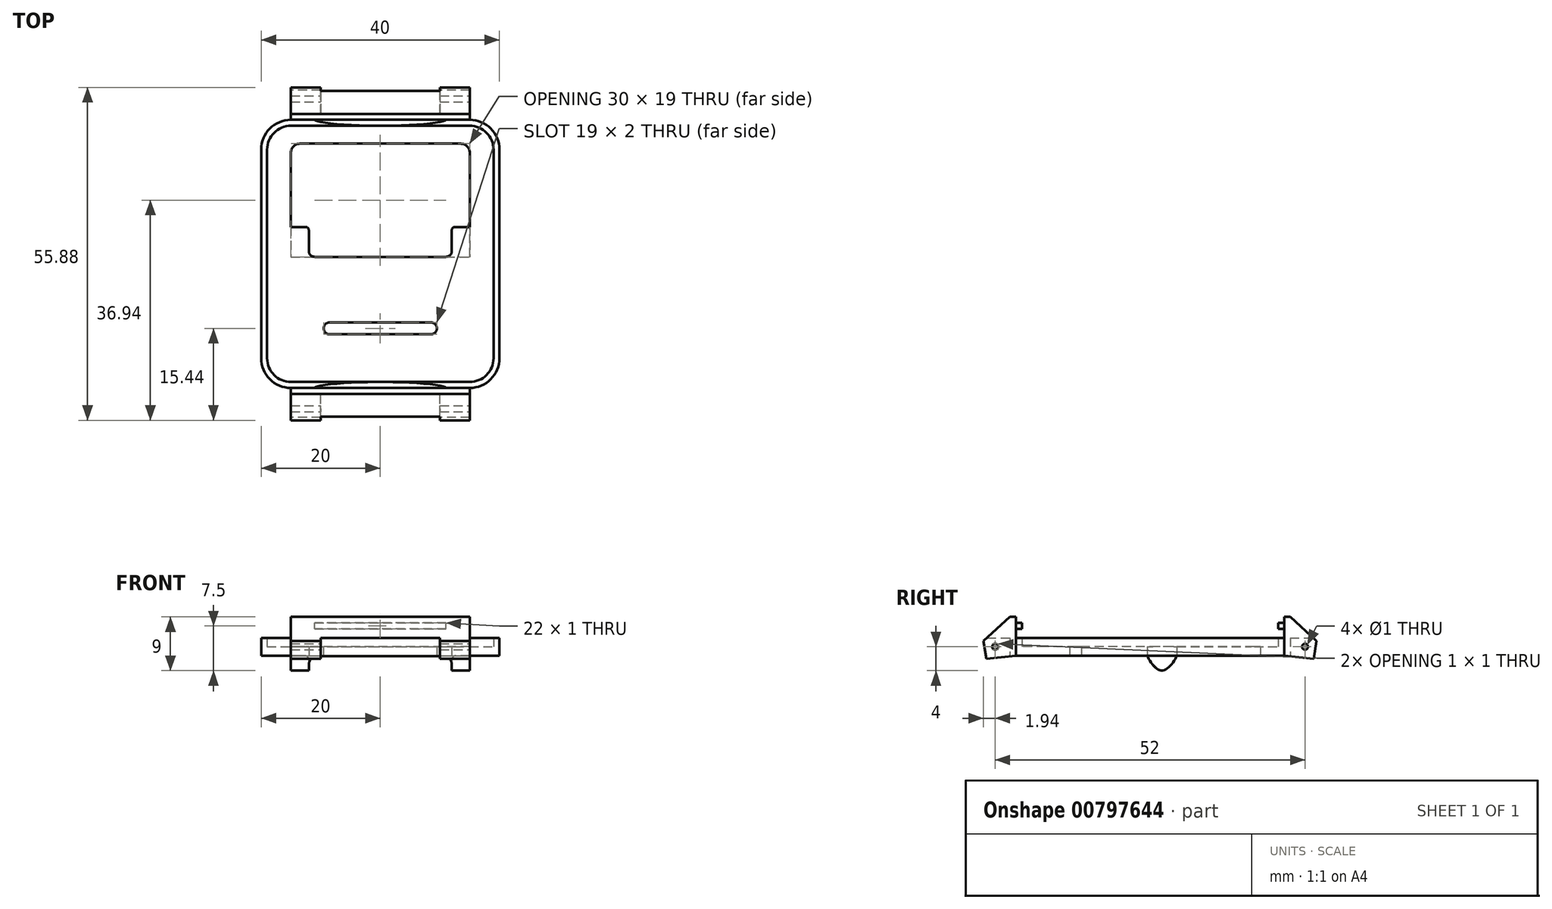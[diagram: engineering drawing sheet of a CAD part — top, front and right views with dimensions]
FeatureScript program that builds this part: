
annotation { "Feature Type Name" : "Feature", "Feature Type Description" : "" }
export const myFeature = defineFeature(function(context is Context, id is Id, definition is map)
    precondition{}
    {
        {
            var Q0;
            Q0=qCreatedBy(makeId("Top.planeOp"),FACE);
            var sketch = newSketch(context, id + "F0", { "sketchPlane" : qUnion([Q0])});
            skLineSegment(sketch, "E0.bottom", {"start": v(-20, -22.5) * mm, "end": v(20, -22.5) * mm});
            skLineSegment(sketch, "E0.top", {"start": v(-20, 22.5) * mm, "end": v(20, 22.5) * mm});
            skLineSegment(sketch, "E0.left", {"start": v(-20, -22.5) * mm, "end": v(-20, 22.5) * mm});
            skLineSegment(sketch, "E0.right", {"start": v(20, -22.5) * mm, "end": v(20, 22.5) * mm});
            skPoint(sketch, "E1", {"position": v(0, 22.5) * mm});
            skPoint(sketch, "E2", {"position": v(20, 0) * mm});
            skLineSegment(sketch, "E3.bottom", {"start": v(-15, 4.5) * mm, "end": v(15, 4.5) * mm});
            skLineSegment(sketch, "E3.top", {"start": v(-15, 18.5) * mm, "end": v(15, 18.5) * mm});
            skLineSegment(sketch, "E3.left", {"start": v(-15, 4.5) * mm, "end": v(-15, 18.5) * mm});
            skLineSegment(sketch, "E3.right", {"start": v(15, 4.5) * mm, "end": v(15, 18.5) * mm});
            skLineSegment(sketch, "E4.bottom", {"start": v(-9.5, -13.5) * mm, "end": v(9.5, -13.5) * mm});
            skLineSegment(sketch, "E4.top", {"start": v(-9.5, -11.5) * mm, "end": v(9.5, -11.5) * mm});
            skLineSegment(sketch, "E4.left", {"start": v(-9.5, -13.5) * mm, "end": v(-9.5, -11.5) * mm});
            skLineSegment(sketch, "E4.right", {"start": v(9.5, -13.5) * mm, "end": v(9.5, -11.5) * mm});
            skPoint(sketch, "E5", {"position": v(0, -11.5) * mm});
            skLineSegment(sketch, "E6.bottom", {"start": v(-12, 4.5) * mm, "end": v(12, 4.5) * mm});
            skLineSegment(sketch, "E6.top", {"start": v(-12, -0.5) * mm, "end": v(12, -0.5) * mm});
            skLineSegment(sketch, "E6.left", {"start": v(-12, 4.5) * mm, "end": v(-12, -0.5) * mm});
            skLineSegment(sketch, "E6.right", {"start": v(12, 4.5) * mm, "end": v(12, -0.5) * mm});
            skLineSegment(sketch, "E7.bottom", {"start": v(-15, 4.5) * mm, "end": v(-12, 4.5) * mm});
            skLineSegment(sketch, "E7.top", {"start": v(-15, -0.5) * mm, "end": v(-12, -0.5) * mm});
            skLineSegment(sketch, "E7.left", {"start": v(-15, 4.5) * mm, "end": v(-15, -0.5) * mm});
            skLineSegment(sketch, "E8.bottom", {"start": v(12, -0.5) * mm, "end": v(15, -0.5) * mm});
            skLineSegment(sketch, "E8.top", {"start": v(12, 4.5) * mm, "end": v(15, 4.5) * mm});
            skLineSegment(sketch, "E8.left", {"start": v(12, -0.5) * mm, "end": v(12, 4.5) * mm});
            skLineSegment(sketch, "E8.right", {"start": v(15, -0.5) * mm, "end": v(15, 4.5) * mm});
            skSolve(sketch);
        }
        {
            var Q0;
            Q0=makeQuery(id+"F0.imprint","IMPRINT",FACE,{"disambiguationData":[TD([[makeQuery(id+"F0.imprint","IMPRINT",EDGE,{"derivedFrom":sQuery(id+"F0.wireOp",EDGE,"E0.bottom")}),1.0]])]});
            var Q1;
            {var subQ0=sQuery(id+"F0.wireOp",EDGE,"E6.left");Q1=makeQuery(id+"F0.imprint","IMPRINT",FACE,{"disambiguationData":[TD([[makeQuery(id+"F0.imprint","IMPRINT",EDGE,{"derivedFrom":subQ0}),-1.0]])]});}
            var Q2;
            {var subQ2=sQuery(id+"F0.wireOp",EDGE,"E6.right");Q2=makeQuery(id+"F0.imprint","IMPRINT",FACE,{"disambiguationData":[TD([[makeQuery(id+"F0.imprint","IMPRINT",EDGE,{"derivedFrom":subQ2}),1.0]])]});}
            extrude(context, id + "F1", {"entities" : qUnion([Q0, Q1, Q2]), "depth" : 1.5 * mm, "offsetDistance" : 25 * mm});
        }
        {
            var Q0;
            {var subQ2=sQuery(id+"F0.wireOp",EDGE,"E6.right");Q0=makeQuery(id+"F0.imprint","IMPRINT",FACE,{"disambiguationData":[TD([[makeQuery(id+"F0.imprint","IMPRINT",EDGE,{"derivedFrom":subQ2}),1.0]])]});}
            var Q1;
            {var subQ0=sQuery(id+"F0.wireOp",EDGE,"E6.left");Q1=makeQuery(id+"F0.imprint","IMPRINT",FACE,{"disambiguationData":[TD([[makeQuery(id+"F0.imprint","IMPRINT",EDGE,{"derivedFrom":subQ0}),-1.0]])]});}
            extrude(context, id + "F2", {"entities" : qUnion([Q0, Q1]), "operationType" : NewBodyOperationType.ADD, "oppositeDirection" : true, "depth" : 2.5 * mm, "offsetDistance" : 25 * mm});
        }
        {
            var Q0;
            Q0=makeQuery(id+"F2.opExtrude","SWEPT_FACE",FACE,{"disambiguationData":[OSD([sQuery(id+"F0.wireOp",EDGE,"E7.left")])]});
            var sketch = newSketch(context, id + "F3", { "sketchPlane" : qUnion([Q0])});
            skPoint(sketch, "E9", {"position": v(-2, -2.5) * mm});
            skPoint(sketch, "E10", {"position": v(-4.5, 0) * mm});
            skPoint(sketch, "E11", {"position": v(0.5, 0) * mm});
            skPoint(sketch, "E12", {"position": v(-2, 4.5) * mm});
            skPoint(sketch, "E12.positionSnap0", {"position": v(-2, 0) * mm});
            skPoint(sketch, "E13", {"position": v(0.5, 2) * mm});
            skPoint(sketch, "E14", {"position": v(-4.5, 2) * mm});
            skFitSpline(sketch, "E15", {"points": [v(-4.5, 0) * mm, v(-2, -2.5) * mm, v(0.5, 0) * mm, v(0.5, 2) * mm, v(-2, 4.5) * mm, v(-4.5, 2) * mm, v(-4.5, 0) * mm]});
            skSolve(sketch);
        }
        {
            var Q0;
            {var subQ1=sQuery(id+"F0.wireOp",EDGE,"E7.left");var subQ2=makeQuery(id+"F2.opExtrude","SWEPT_EDGE",EDGE,{"disambiguationData":[OSD([sQuery(id+"F0.wireOp",EDGE,"E3.bottom"),sQuery(id+"F0.wireOp",EDGE,"E3.left"),subQ1])]});Q0=makeQuery(id+"F3.imprint","IMPRINT",FACE,{"disambiguationData":[TD([[makeQuery(id+"F3.imprint","IMPRINT",EDGE,{"derivedFrom":subQ2}),-1.0]])]});}
            var Q1;
            {var subQ1=sQuery(id+"F0.wireOp",EDGE,"E7.left");var subQ2=makeQuery(id+"F2.opExtrude","SWEPT_EDGE",EDGE,{"disambiguationData":[OSD([sQuery(id+"F0.wireOp",EDGE,"E7.top"),subQ1])]});Q1=makeQuery(id+"F3.imprint","IMPRINT",FACE,{"disambiguationData":[TD([[makeQuery(id+"F3.imprint","IMPRINT",EDGE,{"derivedFrom":subQ2}),1.0]])]});}
            extrude(context, id + "F4", {"entities" : qUnion([Q0, Q1]), "operationType" : NewBodyOperationType.REMOVE, "oppositeDirection" : true, "depth" : 50 * mm, "offsetDistance" : 25 * mm});
        }
        {
            var Q0;
            Q0=makeQuery(id+"F1.opExtrude","SWEPT_EDGE",EDGE,{"disambiguationData":[OSD([sQuery(id+"F0.wireOp",EDGE,"E4.top"),sQuery(id+"F0.wireOp",EDGE,"E4.right")])]});
            var Q1;
            Q1=makeQuery(id+"F1.opExtrude","SWEPT_EDGE",EDGE,{"disambiguationData":[OSD([sQuery(id+"F0.wireOp",EDGE,"E4.bottom"),sQuery(id+"F0.wireOp",EDGE,"E4.right")])]});
            var Q2;
            Q2=makeQuery(id+"F1.opExtrude","SWEPT_EDGE",EDGE,{"disambiguationData":[OSD([sQuery(id+"F0.wireOp",EDGE,"E4.top"),sQuery(id+"F0.wireOp",EDGE,"E4.left")])]});
            var Q3;
            Q3=makeQuery(id+"F1.opExtrude","SWEPT_EDGE",EDGE,{"disambiguationData":[OSD([sQuery(id+"F0.wireOp",EDGE,"E4.bottom"),sQuery(id+"F0.wireOp",EDGE,"E4.left")])]});
            fillet(context, id + "F5", {"entities" : qUnion([Q0, Q1, Q2, Q3]), "radius" : 1 * mm, "tangentPropagation" : true, "allowEdgeOverflow" : false});
        }
        {
            var Q0;
            Q0=makeQuery(id+"F1.opExtrude","SWEPT_EDGE",EDGE,{"disambiguationData":[OSD([sQuery(id+"F0.wireOp",EDGE,"E3.top"),sQuery(id+"F0.wireOp",EDGE,"E3.left")])]});
            var Q1;
            Q1=makeQuery(id+"F1.opExtrude","SWEPT_EDGE",EDGE,{"disambiguationData":[OSD([sQuery(id+"F0.wireOp",EDGE,"E3.top"),sQuery(id+"F0.wireOp",EDGE,"E3.right")])]});
            fillet(context, id + "F6", {"entities" : qUnion([Q0, Q1]), "radius" : 1.5 * mm, "tangentPropagation" : true, "allowEdgeOverflow" : false});
        }
        {
            var Q0;
            Q0=makeQuery(id+"F1.opExtrude","SWEPT_EDGE",EDGE,{"disambiguationData":[OSD([sQuery(id+"F0.wireOp",EDGE,"E6.top"),sQuery(id+"F0.wireOp",EDGE,"E6.right"),sQuery(id+"F0.wireOp",EDGE,"E8.bottom")])]});
            var Q1;
            Q1=makeQuery(id+"F1.opExtrude","SWEPT_EDGE",EDGE,{"disambiguationData":[OSD([sQuery(id+"F0.wireOp",EDGE,"E6.top"),sQuery(id+"F0.wireOp",EDGE,"E6.left"),sQuery(id+"F0.wireOp",EDGE,"E7.top")])]});
            fillet(context, id + "F7", {"entities" : qUnion([Q0, Q1]), "radius" : 1 * mm, "tangentPropagation" : true, "allowEdgeOverflow" : false});
        }
        {
            var Q0;
            {var subQ0=sQuery(id+"F0.wireOp",EDGE,"E6.right");var subQ1=sQuery(id+"F0.wireOp",EDGE,"E3.bottom");Q0=makeQuery(id+"F2.boolean.opBoolean","MERGE",EDGE,{"derivedFrom":[makeQuery(id+"F1.opExtrude","SWEPT_EDGE",EDGE,{"disambiguationData":[OSD([subQ1,subQ0])]}),makeQuery(id+"F2.opExtrude","SWEPT_EDGE",EDGE,{"disambiguationData":[OSD([subQ1,subQ0])]})]});}
            var Q1;
            {var subQ0=sQuery(id+"F0.wireOp",EDGE,"E6.left");var subQ1=sQuery(id+"F0.wireOp",EDGE,"E3.bottom");Q1=makeQuery(id+"F2.boolean.opBoolean","MERGE",EDGE,{"derivedFrom":[makeQuery(id+"F1.opExtrude","SWEPT_EDGE",EDGE,{"disambiguationData":[OSD([subQ1,subQ0])]}),makeQuery(id+"F2.opExtrude","SWEPT_EDGE",EDGE,{"disambiguationData":[OSD([subQ1,subQ0])]})]});}
            fillet(context, id + "F8", {"entities" : qUnion([Q0, Q1]), "radius" : 0.5 * mm, "tangentPropagation" : true, "allowEdgeOverflow" : false});
        }
        {
            var Q0;
            Q0=qCreatedBy(makeId("Top.planeOp"),FACE);
            var sketch = newSketch(context, id + "F9", { "sketchPlane" : qUnion([Q0])});
            skLineSegment(sketch, "E16.bottom", {"start": v(-20, -22.5) * mm, "end": v(20, -22.5) * mm});
            skLineSegment(sketch, "E16.top", {"start": v(-20, 22.5) * mm, "end": v(20, 22.5) * mm});
            skLineSegment(sketch, "E16.left", {"start": v(-20, -22.5) * mm, "end": v(-20, 22.5) * mm});
            skLineSegment(sketch, "E16.right", {"start": v(20, -22.5) * mm, "end": v(20, 22.5) * mm});
            skPoint(sketch, "E17", {"position": v(0, 22.5) * mm});
            skPoint(sketch, "E18.positionSnap0", {"position": v(20, 0) * mm});
            skLineSegment(sketch, "E19.bottom", {"start": v(-19, -21.5) * mm, "end": v(19, -21.5) * mm});
            skLineSegment(sketch, "E19.top", {"start": v(-19, 21.5) * mm, "end": v(19, 21.5) * mm});
            skLineSegment(sketch, "E19.left", {"start": v(-19, -21.5) * mm, "end": v(-19, 21.5) * mm});
            skLineSegment(sketch, "E19.right", {"start": v(19, -21.5) * mm, "end": v(19, 21.5) * mm});
            skSolve(sketch);
        }
        {
            var Q0;
            Q0 = qSketchRegion(id + "F9", true);
            extrude(context, id + "F10", {"entities" : qUnion([Q0]), "operationType" : NewBodyOperationType.ADD, "depth" : 3 * mm, "offsetDistance" : 25 * mm});
        }
        {
            var Q0;
            Q0=makeQuery(id+"F10.opExtrude","SWEPT_EDGE",EDGE,{"disambiguationData":[OSD([sQuery(id+"F9.wireOp",EDGE,"E19.top"),sQuery(id+"F9.wireOp",EDGE,"E19.left")])]});
            var Q1;
            Q1=makeQuery(id+"F10.opExtrude","SWEPT_EDGE",EDGE,{"disambiguationData":[OSD([sQuery(id+"F9.wireOp",EDGE,"E19.top"),sQuery(id+"F9.wireOp",EDGE,"E19.right")])]});
            var Q2;
            Q2=makeQuery(id+"F10.opExtrude","SWEPT_EDGE",EDGE,{"disambiguationData":[OSD([sQuery(id+"F9.wireOp",EDGE,"E19.bottom"),sQuery(id+"F9.wireOp",EDGE,"E19.right")])]});
            var Q3;
            Q3=makeQuery(id+"F10.opExtrude","SWEPT_EDGE",EDGE,{"disambiguationData":[OSD([sQuery(id+"F9.wireOp",EDGE,"E19.bottom"),sQuery(id+"F9.wireOp",EDGE,"E19.left")])]});
            fillet(context, id + "F11", {"entities" : qUnion([Q0, Q1, Q2, Q3]), "radius" : 4 * mm, "tangentPropagation" : true, "allowEdgeOverflow" : false});
        }
        {
            var Q0;
            Q0=makeQuery(id+"F10.boolean.opBoolean","MERGE",EDGE,{"derivedFrom":[makeQuery(id+"F1.opExtrude","SWEPT_EDGE",EDGE,{"disambiguationData":[OSD([sQuery(id+"F0.wireOp",EDGE,"E0.bottom"),sQuery(id+"F0.wireOp",EDGE,"E0.left")])]}),makeQuery(id+"F10.opExtrude","SWEPT_EDGE",EDGE,{"disambiguationData":[OSD([sQuery(id+"F9.wireOp",EDGE,"E16.bottom"),sQuery(id+"F9.wireOp",EDGE,"E16.left")])]})]});
            var Q1;
            Q1=makeQuery(id+"F10.boolean.opBoolean","MERGE",EDGE,{"derivedFrom":[makeQuery(id+"F1.opExtrude","SWEPT_EDGE",EDGE,{"disambiguationData":[OSD([sQuery(id+"F0.wireOp",EDGE,"E0.bottom"),sQuery(id+"F0.wireOp",EDGE,"E0.right")])]}),makeQuery(id+"F10.opExtrude","SWEPT_EDGE",EDGE,{"disambiguationData":[OSD([sQuery(id+"F9.wireOp",EDGE,"E16.bottom"),sQuery(id+"F9.wireOp",EDGE,"E16.right")])]})]});
            var Q2;
            Q2=makeQuery(id+"F10.boolean.opBoolean","MERGE",EDGE,{"derivedFrom":[makeQuery(id+"F1.opExtrude","SWEPT_EDGE",EDGE,{"disambiguationData":[OSD([sQuery(id+"F0.wireOp",EDGE,"E0.top"),sQuery(id+"F0.wireOp",EDGE,"E0.right")])]}),makeQuery(id+"F10.opExtrude","SWEPT_EDGE",EDGE,{"disambiguationData":[OSD([sQuery(id+"F9.wireOp",EDGE,"E16.top"),sQuery(id+"F9.wireOp",EDGE,"E16.right")])]})]});
            var Q3;
            Q3=makeQuery(id+"F10.boolean.opBoolean","MERGE",EDGE,{"derivedFrom":[makeQuery(id+"F1.opExtrude","SWEPT_EDGE",EDGE,{"disambiguationData":[OSD([sQuery(id+"F0.wireOp",EDGE,"E0.top"),sQuery(id+"F0.wireOp",EDGE,"E0.left")])]}),makeQuery(id+"F10.opExtrude","SWEPT_EDGE",EDGE,{"disambiguationData":[OSD([sQuery(id+"F9.wireOp",EDGE,"E16.top"),sQuery(id+"F9.wireOp",EDGE,"E16.left")])]})]});
            fillet(context, id + "F12", {"entities" : qUnion([Q0, Q1, Q2, Q3]), "radius" : 5 * mm, "tangentPropagation" : true, "allowEdgeOverflow" : false});
        }
        {
            var Q0;
            Q0=qCreatedBy(makeId("Right.planeOp"),FACE);
            var sketch = newSketch(context, id + "F13", { "sketchPlane" : qUnion([Q0])});
            skLineSegment(sketch, "E20", {"start": v(22.5, 0) * mm, "end": v(-22.5, 0) * mm, "construction": true});
            skPoint(sketch, "E21", {"position": v(0, 0) * mm});
            skLineSegment(sketch, "E22", {"start": v(22.5, 0) * mm, "end": v(27.47, -0.5) * mm});
            skLineSegment(sketch, "E23", {"start": v(22.5, 0) * mm, "end": v(22.5, 6.5) * mm});
            skLineSegment(sketch, "E24", {"start": v(22.5, 6.5) * mm, "end": v(23.5, 6.5) * mm});
            skLineSegment(sketch, "E25", {"start": v(23.5, 6.5) * mm, "end": v(27.94, 2.46) * mm});
            skLineSegment(sketch, "E26", {"start": v(27.47, -0.5) * mm, "end": v(27.94, 2.46) * mm});
            skLineSegment(sketch, "E27", {"start": v(-22.5, 0) * mm, "end": v(-27.47, -0.5) * mm});
            skLineSegment(sketch, "E28", {"start": v(-27.47, -0.5) * mm, "end": v(-27.94, 2.46) * mm});
            skLineSegment(sketch, "E29", {"start": v(-22.5, 0) * mm, "end": v(-22.5, 6.5) * mm});
            skLineSegment(sketch, "E30", {"start": v(-22.5, 6.5) * mm, "end": v(-23.5, 6.5) * mm});
            skLineSegment(sketch, "E31", {"start": v(-23.5, 6.5) * mm, "end": v(-27.94, 2.46) * mm});
            skSolve(sketch);
        }
        {
            var Q0;
            Q0 = qSketchRegion(id + "F13", true);
            extrude(context, id + "F14", {"entities" : qUnion([Q0]), "operationType" : NewBodyOperationType.ADD, "depth" : 15 * mm, "offsetDistance" : 25 * mm, "hasSecondDirection" : true, "secondDirectionOppositeDirection" : true, "secondDirectionDepth" : 15 * mm});
        }
        {
            var Q0;
            Q0=makeQuery(id+"F14.opExtrude","SWEPT_FACE",FACE,{"disambiguationData":[OSD([sQuery(id+"F13.wireOp",EDGE,"E23")])]});
            var sketch = newSketch(context, id + "F15", { "sketchPlane" : qUnion([Q0])});
            skLineSegment(sketch, "E32.bottom", {"start": v(-11, 4.5) * mm, "end": v(11, 4.5) * mm});
            skLineSegment(sketch, "E32.top", {"start": v(-11, 5.5) * mm, "end": v(11, 5.5) * mm});
            skLineSegment(sketch, "E32.left", {"start": v(-11, 4.5) * mm, "end": v(-11, 5.5) * mm});
            skLineSegment(sketch, "E32.right", {"start": v(11, 4.5) * mm, "end": v(11, 5.5) * mm});
            skPoint(sketch, "E33", {"position": v(0, 4.5) * mm});
            skPoint(sketch, "E34", {"position": v(-11, 5) * mm});
            skSolve(sketch);
        }
        {
            var Q0;
            Q0 = qSketchRegion(id + "F15", true);
            extrude(context, id + "F16", {"entities" : qUnion([Q0]), "operationType" : NewBodyOperationType.ADD, "depth" : 1 * mm, "offsetDistance" : 25 * mm});
        }
        {
            var Q0;
            Q0=makeQuery(id+"F16.opExtrude","SWEPT_FACE",FACE,{"disambiguationData":[OSD([sQuery(id+"F15.wireOp",EDGE,"E32.top")])]});
            var sketch = newSketch(context, id + "F17", { "sketchPlane" : qUnion([Q0])});
            skPoint(sketch, "E35", {"position": v(0, 21.5) * mm});
            skPoint(sketch, "E36", {"position": v(-11, 22.5) * mm});
            skPoint(sketch, "E37", {"position": v(11, 22.5) * mm});
            skPoint(sketch, "E38", {"position": v(0, 23.5) * mm});
            skFitSpline(sketch, "E39", {"points": [v(0, 21.5) * mm, v(-11, 22.5) * mm, v(0, 23.5) * mm, v(11, 22.5) * mm, v(0, 21.5) * mm]});
            skSolve(sketch);
        }
        {
            var Q0;
            {var subQ1=sQuery(id+"F15.wireOp",EDGE,"E32.top");var subQ2=makeQuery(id+"F16.opExtrude","SWEPT_EDGE",EDGE,{"disambiguationData":[OSD([subQ1,sQuery(id+"F15.wireOp",EDGE,"E32.left")])]});Q0=makeQuery(id+"F17.imprint","IMPRINT",FACE,{"disambiguationData":[TD([[makeQuery(id+"F17.imprint","IMPRINT",EDGE,{"derivedFrom":subQ2}),-1.0]])]});}
            var Q1;
            {var subQ1=sQuery(id+"F15.wireOp",EDGE,"E32.top");var subQ2=makeQuery(id+"F16.opExtrude","SWEPT_EDGE",EDGE,{"disambiguationData":[OSD([subQ1,sQuery(id+"F15.wireOp",EDGE,"E32.right")])]});Q1=makeQuery(id+"F17.imprint","IMPRINT",FACE,{"disambiguationData":[TD([[makeQuery(id+"F17.imprint","IMPRINT",EDGE,{"derivedFrom":subQ2}),1.0]])]});}
            extrude(context, id + "F18", {"entities" : qUnion([Q0, Q1]), "operationType" : NewBodyOperationType.REMOVE, "oppositeDirection" : true, "depth" : 1 * mm, "offsetDistance" : 25 * mm});
        }
        {
            var Q0;
            Q0=makeQuery(id+"F14.opExtrude","SWEPT_FACE",FACE,{"disambiguationData":[OSD([sQuery(id+"F13.wireOp",EDGE,"E29")])]});
            var sketch = newSketch(context, id + "F19", { "sketchPlane" : qUnion([Q0])});
            skLineSegment(sketch, "E40.bottom", {"start": v(-11, 4.5) * mm, "end": v(11, 4.5) * mm});
            skLineSegment(sketch, "E40.top", {"start": v(-11, 5.5) * mm, "end": v(11, 5.5) * mm});
            skLineSegment(sketch, "E40.left", {"start": v(-11, 4.5) * mm, "end": v(-11, 5.5) * mm});
            skLineSegment(sketch, "E40.right", {"start": v(11, 4.5) * mm, "end": v(11, 5.5) * mm});
            skPoint(sketch, "E41", {"position": v(0, 4.5) * mm});
            skPoint(sketch, "E42", {"position": v(-11, 5) * mm});
            skSolve(sketch);
        }
        {
            var Q0;
            Q0 = qSketchRegion(id + "F19", true);
            extrude(context, id + "F20", {"entities" : qUnion([Q0]), "operationType" : NewBodyOperationType.ADD, "depth" : 1 * mm, "offsetDistance" : 25 * mm});
        }
        {
            var Q0;
            Q0=makeQuery(id+"F20.opExtrude","SWEPT_FACE",FACE,{"disambiguationData":[OSD([sQuery(id+"F19.wireOp",EDGE,"E40.top")])]});
            var sketch = newSketch(context, id + "F21", { "sketchPlane" : qUnion([Q0])});
            skPoint(sketch, "E43", {"position": v(0, -21.5) * mm});
            skPoint(sketch, "E44", {"position": v(11, -22.5) * mm});
            skPoint(sketch, "E45", {"position": v(-11, -22.5) * mm});
            skPoint(sketch, "E46", {"position": v(0, -23.5) * mm});
            skFitSpline(sketch, "E47", {"points": [v(0, -21.5) * mm, v(11, -22.5) * mm, v(0, -23.5) * mm, v(-11, -22.5) * mm, v(0, -21.5) * mm]});
            skSolve(sketch);
        }
        {
            var Q0;
            {var subQ1=sQuery(id+"F19.wireOp",EDGE,"E40.top");var subQ2=makeQuery(id+"F20.opExtrude","SWEPT_EDGE",EDGE,{"disambiguationData":[OSD([subQ1,sQuery(id+"F19.wireOp",EDGE,"E40.left")])]});Q0=makeQuery(id+"F21.imprint","IMPRINT",FACE,{"disambiguationData":[TD([[makeQuery(id+"F21.imprint","IMPRINT",EDGE,{"derivedFrom":subQ2}),-1.0]])]});}
            var Q1;
            {var subQ1=sQuery(id+"F19.wireOp",EDGE,"E40.top");var subQ2=makeQuery(id+"F20.opExtrude","SWEPT_EDGE",EDGE,{"disambiguationData":[OSD([subQ1,sQuery(id+"F19.wireOp",EDGE,"E40.right")])]});Q1=makeQuery(id+"F21.imprint","IMPRINT",FACE,{"disambiguationData":[TD([[makeQuery(id+"F21.imprint","IMPRINT",EDGE,{"derivedFrom":subQ2}),1.0]])]});}
            extrude(context, id + "F22", {"entities" : qUnion([Q0, Q1]), "operationType" : NewBodyOperationType.REMOVE, "oppositeDirection" : true, "depth" : 1 * mm, "offsetDistance" : 25 * mm});
        }
        {
            var Q0;
            Q0=makeQuery(id+"F14.opExtrude","CAP_FACE",FACE,{"disambiguationData":[OSD([sQuery(id+"F13.wireOp",EDGE,"E22"),sQuery(id+"F13.wireOp",EDGE,"E23"),sQuery(id+"F13.wireOp",EDGE,"E24"),sQuery(id+"F13.wireOp",EDGE,"E25"),sQuery(id+"F13.wireOp",EDGE,"E26")])],"isStart":false});
            var sketch = newSketch(context, id + "F23", { "sketchPlane" : qUnion([Q0])});
            skPoint(sketch, "E48", {"position": v(22.5, 1.5) * mm});
            skLineSegment(sketch, "E49", {"start": v(22.5, 1.5) * mm, "end": v(26, 1.5) * mm, "construction": true});
            skCircle(sketch, "E50", {"center": v(26, 1.5) * mm, "radius": 0.5 * mm});
            skSolve(sketch);
        }
        {
            var Q0;
            Q0 = qSketchRegion(id + "F23", true);
            extrude(context, id + "F24", {"entities" : qUnion([Q0]), "operationType" : NewBodyOperationType.REMOVE, "oppositeDirection" : true, "depth" : 30 * mm, "offsetDistance" : 25 * mm});
        }
        {
            var Q0;
            Q0=makeQuery(id+"F14.opExtrude","CAP_FACE",FACE,{"disambiguationData":[OSD([sQuery(id+"F13.wireOp",EDGE,"E27"),sQuery(id+"F13.wireOp",EDGE,"E28"),sQuery(id+"F13.wireOp",EDGE,"E29"),sQuery(id+"F13.wireOp",EDGE,"E30"),sQuery(id+"F13.wireOp",EDGE,"E31")])],"isStart":false});
            var sketch = newSketch(context, id + "F25", { "sketchPlane" : qUnion([Q0])});
            skPoint(sketch, "E51", {"position": v(-22.5, 1.5) * mm});
            skLineSegment(sketch, "E52", {"start": v(-22.5, 1.5) * mm, "end": v(-26, 1.5) * mm, "construction": true});
            skCircle(sketch, "E53", {"center": v(-26, 1.5) * mm, "radius": 0.5 * mm});
            skSolve(sketch);
        }
        {
            var Q0;
            Q0 = qSketchRegion(id + "F25", true);
            extrude(context, id + "F26", {"entities" : qUnion([Q0]), "operationType" : NewBodyOperationType.REMOVE, "oppositeDirection" : true, "depth" : 30 * mm, "offsetDistance" : 25 * mm});
        }
        {
            var Q0;
            Q0=qCreatedBy(makeId("Top.planeOp"),FACE);
            var sketch = newSketch(context, id + "F27", { "sketchPlane" : qUnion([Q0])});
            skLineSegment(sketch, "E54", {"start": v(0, -23.5) * mm, "end": v(0, 23.5) * mm, "construction": true});
            skPoint(sketch, "E55", {"position": v(0, 0) * mm});
            skLineSegment(sketch, "E56.bottom", {"start": v(-10, 23.5) * mm, "end": v(10, 23.5) * mm});
            skLineSegment(sketch, "E56.top", {"start": v(-10, 29.5) * mm, "end": v(10, 29.5) * mm});
            skLineSegment(sketch, "E56.left", {"start": v(-10, 23.5) * mm, "end": v(-10, 29.5) * mm});
            skLineSegment(sketch, "E56.right", {"start": v(10, 23.5) * mm, "end": v(10, 29.5) * mm});
            skPoint(sketch, "E57", {"position": v(0, 23.5) * mm});
            skLineSegment(sketch, "E58.bottom", {"start": v(-10, -29.5) * mm, "end": v(10, -29.5) * mm});
            skLineSegment(sketch, "E58.top", {"start": v(-10, -23.5) * mm, "end": v(10, -23.5) * mm});
            skLineSegment(sketch, "E58.left", {"start": v(-10, -29.5) * mm, "end": v(-10, -23.5) * mm});
            skLineSegment(sketch, "E58.right", {"start": v(10, -29.5) * mm, "end": v(10, -23.5) * mm});
            skPoint(sketch, "E59", {"position": v(0, -23.5) * mm});
            skSolve(sketch);
        }
        {
            var Q0;
            Q0 = qSketchRegion(id + "F27", true);
            extrude(context, id + "F28", {"entities" : qUnion([Q0]), "operationType" : NewBodyOperationType.REMOVE, "depth" : 3 * mm, "offsetDistance" : 25 * mm, "hasSecondDirection" : true, "secondDirectionOppositeDirection" : true, "secondDirectionDepth" : 2 * mm});
        }
    });
